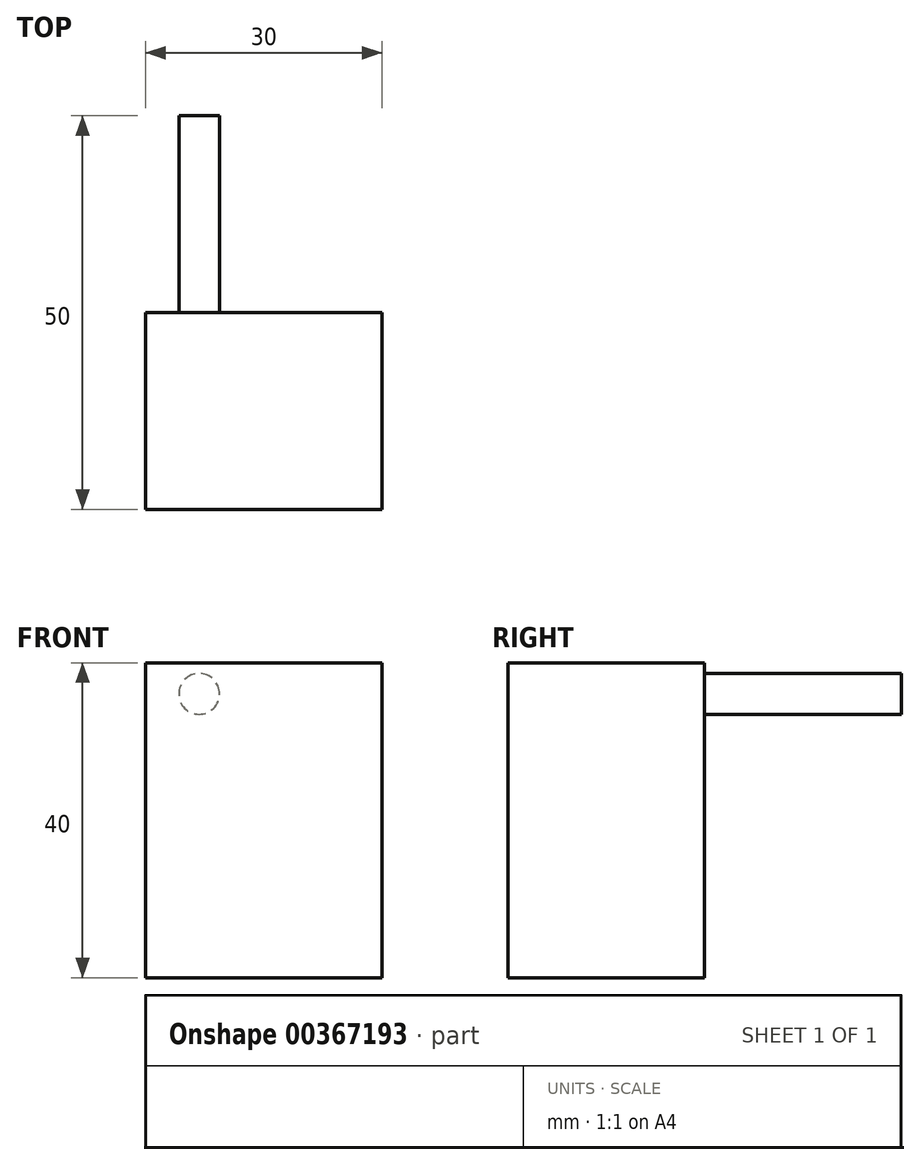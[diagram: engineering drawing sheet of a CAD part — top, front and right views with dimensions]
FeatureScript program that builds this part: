
annotation { "Feature Type Name" : "Feature", "Feature Type Description" : "" }
export const myFeature = defineFeature(function(context is Context, id is Id, definition is map)
    precondition{}
    {
        {
            var Q0;
            Q0=qCreatedBy(makeId("Front.planeOp"),FACE);
            var sketch = newSketch(context, id + "F0", { "sketchPlane" : qUnion([Q0])});
            skLineSegment(sketch, "E0.bottom", {"start": v(0, 0) * mm, "end": v(30, 0) * mm});
            skLineSegment(sketch, "E0.top", {"start": v(0, 40) * mm, "end": v(30, 40) * mm});
            skLineSegment(sketch, "E0.left", {"start": v(0, 0) * mm, "end": v(0, 40) * mm});
            skLineSegment(sketch, "E0.right", {"start": v(30, 0) * mm, "end": v(30, 40) * mm});
            skSolve(sketch);
        }
        {
            var Q0;
            Q0=makeQuery(id+"F0.imprint","IMPRINT",FACE,{"disambiguationData":[TD([[makeQuery(id+"F0.imprint","IMPRINT",EDGE,{"derivedFrom":sQuery(id+"F0.wireOp",EDGE,"E0.bottom")}),1.0]])]});
            extrude(context, id + "F1", {"entities" : qUnion([Q0]), "depth" : 25 * mm});
        }
        {
            var Q0;
            Q0=qCreatedBy(makeId("Front.planeOp"),FACE);
            var sketch = newSketch(context, id + "F2", { "sketchPlane" : qUnion([Q0])});
            skCircle(sketch, "E1", {"center": v(6.8, 36.05) * mm, "radius": 2.58 * mm});
            skSolve(sketch);
        }
        {
            var Q0;
            Q0=makeQuery(id+"F2.imprint","IMPRINT",FACE,{"disambiguationData":[TD([[makeQuery(id+"F2.imprint","IMPRINT",EDGE,{"derivedFrom":sQuery(id+"F2.wireOp",EDGE,"E1")}),1.0]])]});
            extrude(context, id + "F3", {"entities" : qUnion([Q0]), "operationType" : NewBodyOperationType.ADD, "oppositeDirection" : true, "depth" : 25 * mm});
        }
    });
